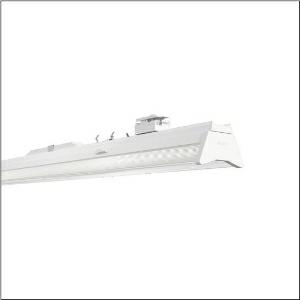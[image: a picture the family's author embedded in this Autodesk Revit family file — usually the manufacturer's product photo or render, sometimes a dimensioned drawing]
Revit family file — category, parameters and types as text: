
# Revit family: licross_21_performance_mo_52td16vn48xg
name_source: partatom
category: Lighting Fixtures
units: mm (PartAtom-declared; Revit-internal decimal feet)

## family parameters
Cut with Voids When Loaded = No
Host = Face
Light Source = No
Part Type = Normal
Room Calculation Point = No
Round Connector Dimension = Use Diameter
Shared = No

## types (1)
- --- (1 x LED, 8000 lm, 44.6 W, 4000K)
    Apparent Load = 45 VA
    CIE Flux Codes = 66 88 96 79 100
    Color Rendering = 80
    Color Temperature = 4000K
    Default Elevation = 1800 mm
    Description = Licross 21 Performance MO, luminaire insert, of sheet steel, galvanised, coil coated, white, length: 1.500mm, width: 120mm, height: 123mm, LED rated luminous flux: 8.000lm, light colour: 840, SDCM (Standard Deviation of Colour Matching)MacAdam ≤ 3 SDCM (initial), control gear: DALI 2, CLO, with plug, 5-pole, with phase selection, mains connection: 220..240V, AC, 50/60Hz, start of lifetime: 45W, end of service life: 53W, internal wiring halogen-free, primary light control with lens, of plastic, primary optical cover: cover, of PMMA, light emission: direct/indirect distribution, primary light characteristic: symmetric, protection rating (complete): IP54, insulation class (complete): insulation class I (protective earthing), certification: CE, ENEC, VDE, UKCA, protection symbol: D if used in an environment with non-conductive dust loads with corresponding accessories, impact resistance: IK06, permissible ambient temperature for indoor applications: -25..+45°C, corresponds to IFS (International Featured Standards) requirements for safety and quality in the food industry, reducing of maximum allowable ambient temperature of 5°C with ceiling mounting, LABS conformity tested according to VDMA 24364:2018-05, The light source and the operating device comply with the requirements of the Ecodesign Regulation (EU) 2019/2020 and are replaceable in accordance with this regulation, packaging unit: 1 piece
    Height = 114 mm
    Lamp = 1 x LED
    Lamp Light Flux = 8000 lm
    Lamp Power = 44.6 W
    Lamp count = 1
    Length = 1500 mm
    Luminous efficacy = 179 lm/W
    Manufacturer = Siteco
    ModVariant = No
    Model = 52TD16VN48XG
    Mounting Place = Ceiling
    Mounting Type = Pendant
    Number of Poles = 1
    OnlyDefault = Yes
    Power Factor = 1
    Product Name = Licross 21 Performance MO
    Product group = luminaire insert | ceiling pendant
    ProductGroupID = 901
    Protection Class = Protection class I
    Protection Degree = IP 54
    RLX_Detail_Level = 1
    RLX_Emergency_Light_Flux = 0 lm
    RLX_Emergency_Type = 0
    RLX_Emergency_Type_DB = No
    RlxData = <blob elided: 34313 chars, md5=b4889d81>
    Socket = socket
    Standby Power = 0 W
    System Light Flux = 8000 lm
    System Power = 45 W
    Type Comments = factory setting: luminous flux: 100 % | dim-lin: 254 | 301 mA
    Type Image = l_1256138.jpg
    URL = http://relux.com
    VarID = @adj_088071
    Voltage = 0 V
    Weight = 0.00 kg
    Width = 120 mm

## geometry (parser evidence)
native form markers: Blend x4, Sweep x12
no freeform markers — native parametric forms only
